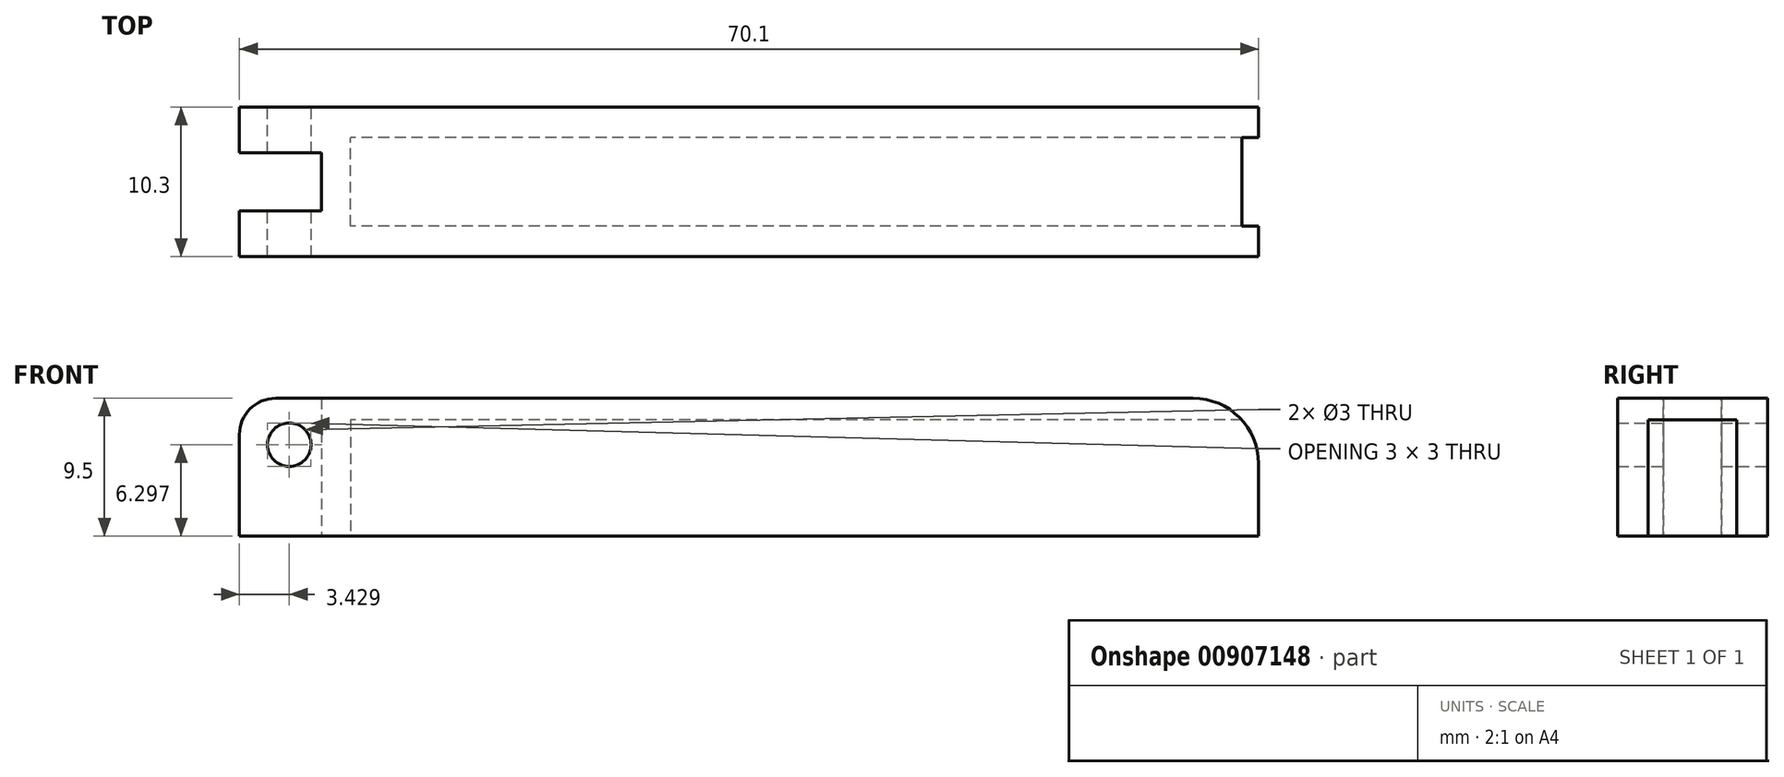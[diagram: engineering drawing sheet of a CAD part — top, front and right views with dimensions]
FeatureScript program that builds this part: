
annotation { "Feature Type Name" : "Feature", "Feature Type Description" : "" }
export const myFeature = defineFeature(function(context is Context, id is Id, definition is map)
    precondition{}
    {
        {
            var Q0;
            Q0=qCreatedBy(makeId("Front.planeOp"),FACE);
            var sketch = newSketch(context, id + "F0", { "sketchPlane" : qUnion([Q0])});
            skLineSegment(sketch, "E0.bottom", {"start": v(-33.9, 29.46) * mm, "end": v(29.2, 29.46) * mm});
            skLineSegment(sketch, "E0.top", {"start": v(-36.4, 19.96) * mm, "end": v(33.7, 19.96) * mm});
            skLineSegment(sketch, "E0.left", {"start": v(-36.4, 26.96) * mm, "end": v(-36.4, 19.96) * mm});
            skLineSegment(sketch, "E0.right", {"start": v(33.7, 24.96) * mm, "end": v(33.7, 19.96) * mm});
            skPoint(sketch, "E1.visualSharp", {"position": v(33.7, 29.46) * mm});
            skArc(sketch, "E1.filletArc", {"start": v(33.7, 24.96) * mm, "mid": v(32.38, 28.14) * mm, "end": v(29.2, 29.46) * mm});
            skPoint(sketch, "E2.visualSharp", {"position": v(-36.4, 29.46) * mm});
            skArc(sketch, "E2.filletArc", {"start": v(-33.9, 29.46) * mm, "mid": v(-35.67, 28.72) * mm, "end": v(-36.4, 26.96) * mm});
            skSolve(sketch);
        }
        {
            var Q0;
            Q0=makeQuery(id+"F0.imprint","IMPRINT",FACE,{"disambiguationData":[TD([[makeQuery(id+"F0.imprint","IMPRINT",EDGE,{"derivedFrom":sQuery(id+"F0.wireOp",EDGE,"E0.bottom")}),-1.0]])]});
            extrude(context, id + "F1", {"entities" : qUnion([Q0]), "depth" : 10.3 * mm, "offsetDistance" : 25 * mm});
        }
        {
            var Q0;
            Q0=qCreatedBy(makeId("Top.planeOp"),FACE);
            var sketch = newSketch(context, id + "F2", { "sketchPlane" : qUnion([Q0])});
            skLineSegment(sketch, "E3.bottom", {"start": v(-36.94, -7.15) * mm, "end": v(-30.74, -7.15) * mm});
            skLineSegment(sketch, "E3.top", {"start": v(-36.94, -3.15) * mm, "end": v(-30.74, -3.15) * mm});
            skLineSegment(sketch, "E3.left", {"start": v(-36.94, -7.15) * mm, "end": v(-36.94, -3.15) * mm});
            skLineSegment(sketch, "E3.right", {"start": v(-30.74, -7.15) * mm, "end": v(-30.74, -3.15) * mm});
            skSolve(sketch);
        }
        {
            var Q0;
            Q0 = qSketchRegion(id + "F2", true);
            extrude(context, id + "F3", {"entities" : qUnion([Q0]), "operationType" : NewBodyOperationType.REMOVE, "endBound" : BoundingType.THROUGH_ALL, "depth" : 42.1 * mm, "offsetDistance" : 25 * mm});
        }
        {
            var Q0;
            Q0=qCreatedBy(makeId("Front.planeOp"),FACE);
            var sketch = newSketch(context, id + "F4", { "sketchPlane" : qUnion([Q0])});
            skCircle(sketch, "E4", {"center": v(-32.97, 26.26) * mm, "radius": 1.5 * mm});
            skSolve(sketch);
        }
        {
            var Q0;
            Q0 = qSketchRegion(id + "F4", true);
            extrude(context, id + "F5", {"entities" : qUnion([Q0]), "operationType" : NewBodyOperationType.REMOVE, "endBound" : BoundingType.THROUGH_ALL, "depth" : 25 * mm, "offsetDistance" : 25 * mm});
        }
        {
            var Q0;
            Q0=makeQuery(id+"F1.opExtrude","SWEPT_FACE",FACE,{"disambiguationData":[OSD([sQuery(id+"F0.wireOp",EDGE,"E0.top")])]});
            var sketch = newSketch(context, id + "F6", { "sketchPlane" : qUnion([Q0])});
            skLineSegment(sketch, "E5.bottom", {"start": v(33.7, 8.2) * mm, "end": v(-28.74, 8.2) * mm});
            skLineSegment(sketch, "E5.top", {"start": v(33.7, 2.1) * mm, "end": v(-28.74, 2.1) * mm});
            skLineSegment(sketch, "E5.left", {"start": v(33.7, 8.2) * mm, "end": v(33.7, 2.1) * mm});
            skLineSegment(sketch, "E5.right", {"start": v(-28.74, 8.2) * mm, "end": v(-28.74, 2.1) * mm});
            skSolve(sketch);
        }
        {
            var Q0;
            Q0 = qSketchRegion(id + "F6", true);
            extrude(context, id + "F7", {"entities" : qUnion([Q0]), "operationType" : NewBodyOperationType.REMOVE, "oppositeDirection" : true, "depth" : 8 * mm, "offsetDistance" : 25 * mm});
        }
    });
